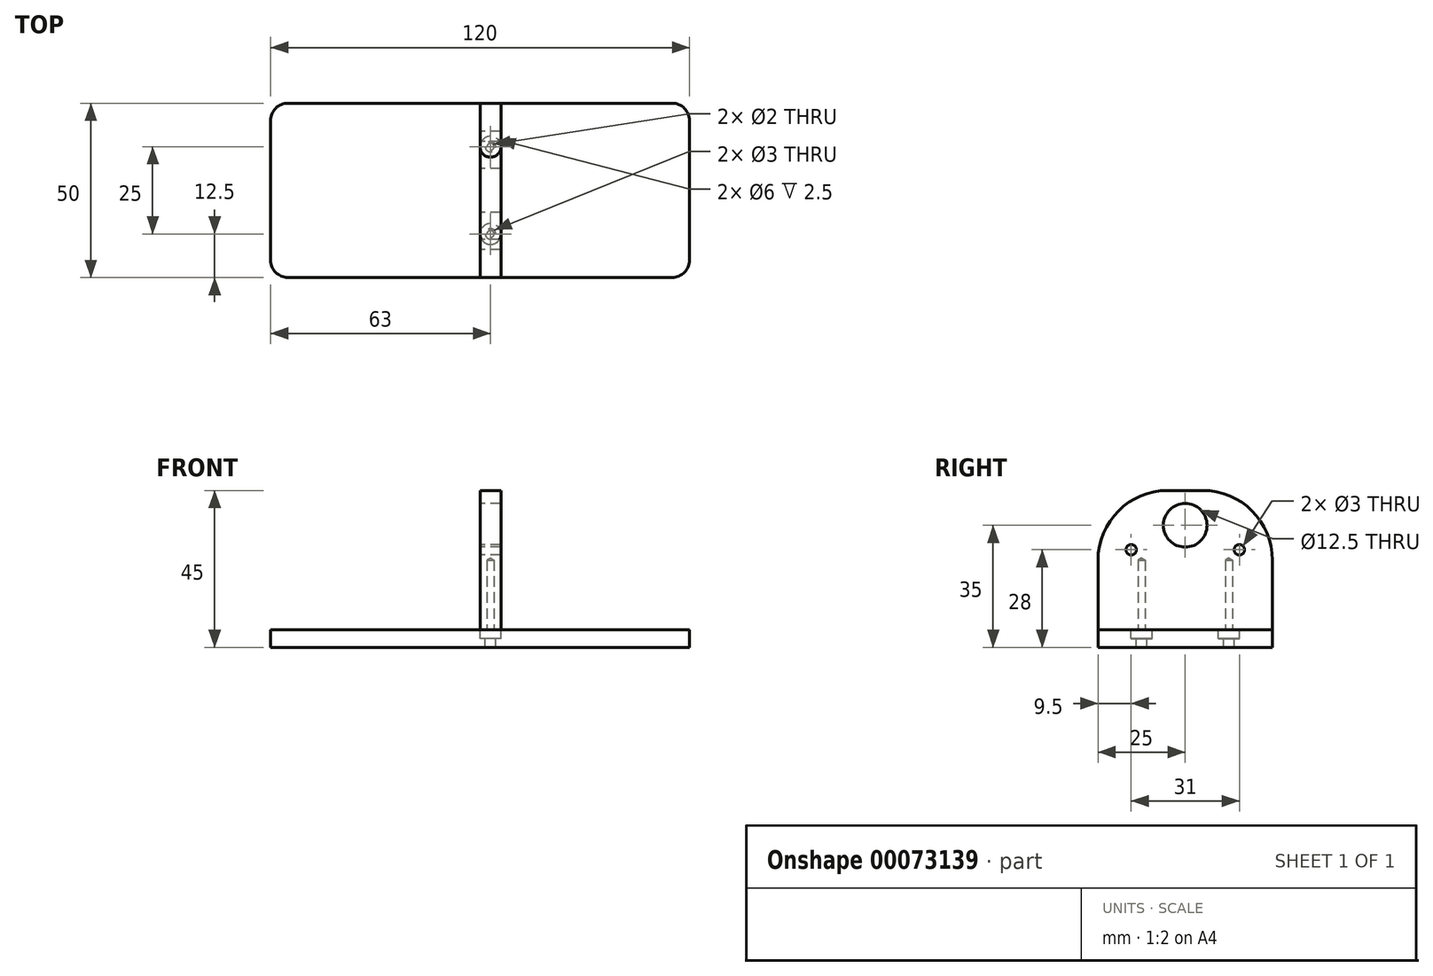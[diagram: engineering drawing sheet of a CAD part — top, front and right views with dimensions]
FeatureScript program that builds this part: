
annotation { "Feature Type Name" : "Feature", "Feature Type Description" : "" }
export const myFeature = defineFeature(function(context is Context, id is Id, definition is map)
    precondition{}
    {
        {
            var Q0;
            Q0=qCreatedBy(makeId("Top.planeOp"),FACE);
            var sketch = newSketch(context, id + "F0", { "sketchPlane" : qUnion([Q0])});
            skLineSegment(sketch, "E0.rect.bottom", {"start": v(-60, 25) * mm, "end": v(60, 25) * mm});
            skLineSegment(sketch, "E0.rect.top", {"start": v(-60, -25) * mm, "end": v(60, -25) * mm});
            skLineSegment(sketch, "E0.rect.left", {"start": v(-60, 25) * mm, "end": v(-60, -25) * mm});
            skLineSegment(sketch, "E0.rect.right", {"start": v(60, 25) * mm, "end": v(60, -25) * mm});
            skPoint(sketch, "E0.rect.middle", {"position": v(0, 0) * mm});
            skSolve(sketch);
        }
        {
            var Q0;
            Q0=makeQuery(id+"F0.imprint","IMPRINT",FACE,{"disambiguationData":[TD([[makeQuery(id+"F0.imprint","IMPRINT",EDGE,{"derivedFrom":sQuery(id+"F0.wireOp",EDGE,"E0.rect.bottom")}),-1.0]])]});
            extrude(context, id + "F1", {"entities" : qUnion([Q0]), "depth" : 5 * mm});
        }
        {
            var Q0;
            Q0=makeQuery(id+"F1.opExtrude","CAP_FACE",FACE,{"disambiguationData":[OSD([sQuery(id+"F0.wireOp",EDGE,"E0.rect.bottom"),sQuery(id+"F0.wireOp",EDGE,"E0.rect.top"),sQuery(id+"F0.wireOp",EDGE,"E0.rect.left"),sQuery(id+"F0.wireOp",EDGE,"E0.rect.right")])],"isStart":false});
            var sketch = newSketch(context, id + "F2", { "sketchPlane" : qUnion([Q0])});
            skLineSegment(sketch, "E1.bottom", {"start": v(0, 25) * mm, "end": v(6, 25) * mm});
            skLineSegment(sketch, "E1.top", {"start": v(0, -25) * mm, "end": v(6, -25) * mm});
            skLineSegment(sketch, "E1.left", {"start": v(0, 25) * mm, "end": v(0, -25) * mm});
            skLineSegment(sketch, "E1.right", {"start": v(6, 25) * mm, "end": v(6, -25) * mm});
            skLineSegment(sketch, "E2", {"start": v(6, 25) * mm, "end": v(0, 0) * mm});
            skPoint(sketch, "E3", {"position": v(3, 12.5) * mm});
            skPoint(sketch, "E4.MirrorP", {"position": v(3, -12.5) * mm});
            skSolve(sketch);
        }
        {
            var Q0;
            Q0=makeQuery(id+"F2.imprint","IMPRINT",FACE,{"disambiguationData":[TD([[makeQuery(id+"F2.imprint","IMPRINT",EDGE,{"derivedFrom":sQuery(id+"F2.wireOp",EDGE,"E1.bottom")}),-1.0]])]});
            var Q1;
            {var subQ0=sQuery(id+"F2.wireOp",EDGE,"E1.top");Q1=makeQuery(id+"F2.imprint","IMPRINT",FACE,{"disambiguationData":[TD([[makeQuery(id+"F2.imprint","IMPRINT",EDGE,{"derivedFrom":subQ0}),1.0]])]});}
            extrude(context, id + "F3", {"entities" : qUnion([Q0, Q1]), "depth" : 40 * mm});
        }
        {
            var Q0;
            Q0=makeQuery(id+"F3.opExtrude","CAP_EDGE",EDGE,{"disambiguationData":[OSD([sQuery(id+"F2.wireOp",EDGE,"E1.top")])],"isStart":false});
            var Q1;
            Q1=makeQuery(id+"F3.opExtrude","CAP_EDGE",EDGE,{"disambiguationData":[OSD([sQuery(id+"F2.wireOp",EDGE,"E1.bottom")])],"isStart":false});
            fillet(context, id + "F4", {"entities" : qUnion([Q0, Q1]), "radius" : 20 * mm, "tangentPropagation" : true, "allowEdgeOverflow" : false});
        }
        {
            var Q0;
            Q0=makeQuery(id+"F3.opExtrude","SWEPT_FACE",FACE,{"disambiguationData":[OSD([sQuery(id+"F2.wireOp",EDGE,"E1.left")])]});
            var sketch = newSketch(context, id + "F5", { "sketchPlane" : qUnion([Q0])});
            skPoint(sketch, "E5", {"position": v(0, 35) * mm});
            skPoint(sketch, "E6", {"position": v(-15.5, 28) * mm});
            skPoint(sketch, "E7.MirrorP", {"position": v(15.5, 28) * mm});
            skSolve(sketch);
        }
        {
            var Q0;
            Q0=sQuery(id+"F5.wireOp",VERTEX,"E5");
            var Q1;
            Q1=makeQuery(id+"F3.opExtrude","SWEPT_BODY",BODY,{"disambiguationData":[OSD([sQuery(id+"F2.wireOp",EDGE,"E1.bottom"),sQuery(id+"F2.wireOp",EDGE,"E1.top"),sQuery(id+"F2.wireOp",EDGE,"E1.left"),sQuery(id+"F2.wireOp",EDGE,"E1.right")])]});
            hole(context, id + "F6", {"style" : HoleStyle.SIMPLE, "holeDiameter" : 12.5 * mm, "endStyle" : HoleEndStyle.THROUGH, "locations" : qUnion([Q0]), "scope" : qUnion([Q1])});
        }
        {
            var Q0;
            Q0=sQuery(id+"F5.wireOp",VERTEX,"E6");
            var Q1;
            Q1=sQuery(id+"F5.wireOp",VERTEX,"E7.MirrorP");
            var Q2;
            Q2=makeQuery(id+"F3.opExtrude","SWEPT_BODY",BODY,{"disambiguationData":[OSD([sQuery(id+"F2.wireOp",EDGE,"E1.bottom"),sQuery(id+"F2.wireOp",EDGE,"E1.top"),sQuery(id+"F2.wireOp",EDGE,"E1.left"),sQuery(id+"F2.wireOp",EDGE,"E1.right")])]});
            hole(context, id + "F7", {"style" : HoleStyle.SIMPLE, "holeDiameter" : 3 * mm, "endStyle" : HoleEndStyle.THROUGH, "locations" : qUnion([Q0, Q1]), "scope" : qUnion([Q2])});
        }
        {
            var Q0;
            Q0=sQuery(id+"F2.wireOp",VERTEX,"E3");
            var Q1;
            Q1=sQuery(id+"F2.wireOp",VERTEX,"E4.MirrorP");
            var Q2;
            Q2=makeQuery(id+"F1.opExtrude","SWEPT_BODY",BODY,{"disambiguationData":[OSD([sQuery(id+"F0.wireOp",EDGE,"E0.rect.bottom"),sQuery(id+"F0.wireOp",EDGE,"E0.rect.top"),sQuery(id+"F0.wireOp",EDGE,"E0.rect.left"),sQuery(id+"F0.wireOp",EDGE,"E0.rect.right")])]});
            hole(context, id + "F8", {"style" : HoleStyle.C_BORE, "holeDiameter" : 3 * mm, "cBoreDiameter" : 6 * mm, "cBoreDepth" : 2.5 * mm, "endStyle" : HoleEndStyle.THROUGH, "locations" : qUnion([Q0, Q1]), "scope" : qUnion([Q2])});
        }
        {
            var Q0;
            Q0=sQuery(id+"F2.wireOp",VERTEX,"E4.MirrorP");
            var Q1;
            Q1=sQuery(id+"F2.wireOp",VERTEX,"E3");
            var Q2;
            Q2=makeQuery(id+"F3.opExtrude","SWEPT_BODY",BODY,{"disambiguationData":[OSD([sQuery(id+"F2.wireOp",EDGE,"E1.bottom"),sQuery(id+"F2.wireOp",EDGE,"E1.top"),sQuery(id+"F2.wireOp",EDGE,"E1.left"),sQuery(id+"F2.wireOp",EDGE,"E1.right")])]});
            hole(context, id + "F9", {"style" : HoleStyle.SIMPLE, "holeDiameter" : 2 * mm, "endStyle" : HoleEndStyle.BLIND, "oppositeDirection" : true, "holeDepth" : 20 * mm, "locations" : qUnion([Q0, Q1]), "scope" : qUnion([Q2])});
        }
        {
            var Q0;
            Q0=makeQuery(id+"F1.opExtrude","SWEPT_EDGE",EDGE,{"disambiguationData":[OSD([sQuery(id+"F0.wireOp",EDGE,"E0.rect.top"),sQuery(id+"F0.wireOp",EDGE,"E0.rect.left")])]});
            var Q1;
            Q1=makeQuery(id+"F1.opExtrude","SWEPT_EDGE",EDGE,{"disambiguationData":[OSD([sQuery(id+"F0.wireOp",EDGE,"E0.rect.bottom"),sQuery(id+"F0.wireOp",EDGE,"E0.rect.left")])]});
            var Q2;
            Q2=makeQuery(id+"F1.opExtrude","SWEPT_EDGE",EDGE,{"disambiguationData":[OSD([sQuery(id+"F0.wireOp",EDGE,"E0.rect.top"),sQuery(id+"F0.wireOp",EDGE,"E0.rect.right")])]});
            var Q3;
            Q3=makeQuery(id+"F1.opExtrude","SWEPT_EDGE",EDGE,{"disambiguationData":[OSD([sQuery(id+"F0.wireOp",EDGE,"E0.rect.bottom"),sQuery(id+"F0.wireOp",EDGE,"E0.rect.right")])]});
            fillet(context, id + "F10", {"entities" : qUnion([Q0, Q1, Q2, Q3]), "radius" : 5 * mm, "tangentPropagation" : true, "allowEdgeOverflow" : false});
        }
    });
